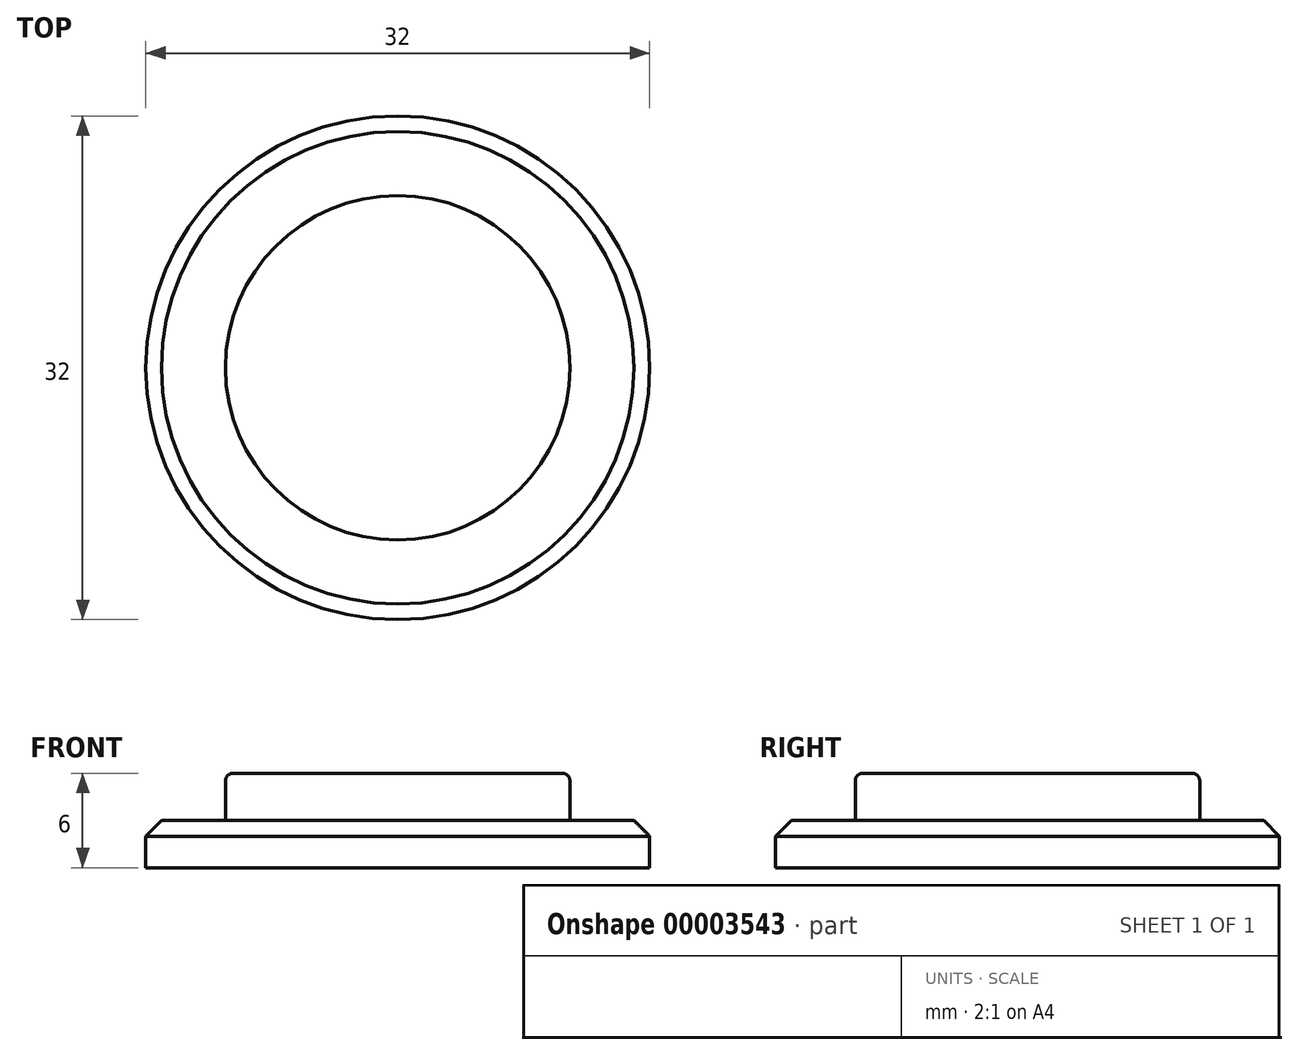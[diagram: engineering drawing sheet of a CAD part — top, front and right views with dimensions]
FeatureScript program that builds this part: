
annotation { "Feature Type Name" : "Feature", "Feature Type Description" : "" }
export const myFeature = defineFeature(function(context is Context, id is Id, definition is map)
    precondition{}
    {
        {
            var Q0;
            Q0=qCreatedBy(makeId("Top.planeOp"),FACE);
            var sketch = newSketch(context, id + "F0", { "sketchPlane" : qUnion([Q0])});
            skCircle(sketch, "E0", {"center": v(0, 0) * mm, "radius": 16 * mm});
            skSolve(sketch);
        }
        {
            var Q0;
            Q0=makeQuery(id+"F0.imprint","IMPRINT",FACE,{"disambiguationData":[TD([[makeQuery(id+"F0.imprint","IMPRINT",EDGE,{"derivedFrom":sQuery(id+"F0.wireOp",EDGE,"E0")}),1.0]])]});
            extrude(context, id + "F1", {"entities" : qUnion([Q0]), "depth" : 3 * mm});
        }
        {
            var Q0;
            Q0=makeQuery(id+"F1.opExtrude","CAP_FACE",FACE,{"disambiguationData":[OSD([sQuery(id+"F0.wireOp",EDGE,"E0")])],"isStart":false});
            var sketch = newSketch(context, id + "F2", { "sketchPlane" : qUnion([Q0])});
            skCircle(sketch, "E1", {"center": v(0, 0) * mm, "radius": 10.94 * mm});
            skSolve(sketch);
        }
        {
            var Q0;
            Q0=makeQuery(id+"F2.imprint","IMPRINT",FACE,{"disambiguationData":[TD([[makeQuery(id+"F2.imprint","IMPRINT",EDGE,{"derivedFrom":sQuery(id+"F2.wireOp",EDGE,"E1")}),1.0]])]});
            extrude(context, id + "F3", {"entities" : qUnion([Q0]), "operationType" : NewBodyOperationType.ADD, "depth" : 3 * mm});
        }
        {
            var Q0;
            Q0=makeQuery(id+"F1.opExtrude","CAP_EDGE",EDGE,{"disambiguationData":[OSD([sQuery(id+"F0.wireOp",EDGE,"E0")])],"isStart":false});
            chamfer(context, id + "F4", {"entities" : qUnion([Q0]), "width" : 1 * mm, "tangentPropagation" : true});
        }
        {
            var Q0;
            Q0=makeQuery(id+"F3.opExtrude","CAP_EDGE",EDGE,{"disambiguationData":[OSD([sQuery(id+"F2.wireOp",EDGE,"E1")])],"isStart":false});
            fillet(context, id + "F5", {"entities" : qUnion([Q0]), "radius" : 0.5 * mm, "tangentPropagation" : true, "allowEdgeOverflow" : false});
        }
    });
